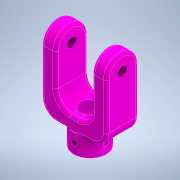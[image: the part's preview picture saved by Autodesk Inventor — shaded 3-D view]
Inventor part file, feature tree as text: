
AUTODESK INVENTOR PART (.ipt)
format: ipt  version: 2022 (Build 260153000, 153)  size: 295,424 bytes
history: native  units: in
note: dims shown in document units (in); Inventor stores cm internally (conversion verified against a paired STEP export)
features: extrude x5, sketch x5, fillet x4, plane x1, other x1, pattern_circular x1
ambient origin geometry x8: Origin, YZ Plane, XZ Plane, XY Plane, X Axis, Y Axis, Z Axis, Center Point
bodies: Solid1 (feature_tree)
feature tree (17):
  extrude  "Extrusion1"  Depth=2.6772in
  fillet  "Fillet1"  Radius=0.5906in
  fillet  "Fillet2"  Radius=0.5906in
  fillet  "Fillet3"  Radius=0.5512in
  extrude  "Extrusion2"  Depth=1.3386in TaperAngle=0.0deg
  extrude  "Extrusion3"  Depth=0.6693in
  fillet  "Fillet4"  Radius=0.5906in
  plane  "Work Plane1"
  extrude  "Extrusion4"  Depth=0.6693in
  other  "Work Axis1"
  pattern_circular  "Circular Pattern1"  Count=2  [1 undecoded]
  extrude  "Extrusion5"  Depth=0.3937in
  sketch  "Sketch1"  dims[d0=3.1496in d1=2.6772in d2=0.5906in d3=0.5906in d4=0.5512in]
  sketch  "Sketch2"  dims[d5=1.4961in d6=1.3386in d7=0.0in]
  sketch  "Sketch3"  dims[d8=0.6693in d9=0.6693in d10=0.5906in]
  sketch  "Sketch4"  dims[d11=1.3386in d12=0.6693in]
  sketch  "Sketch5"  dims[d13=1.3386in d14=0.7874in d15=0.0in d16=0.748in d17=0.0in d18=0.0in d19=0.1181in d20=0.6693in d21=0.2362in d22=0.3937in d23=0.6693in d24=0.0in d25=0.0in d26=1.5748in d27=360.0deg d29=0.3976in d30=0.6496in d31=0.6693in d32=0.0in d33=0.0in]
note: 1 required parameter value undecoded (feature->parameter linkage not recoverable at this tier; creation-order binding heuristic only, values carry confidence <= 0.55)
